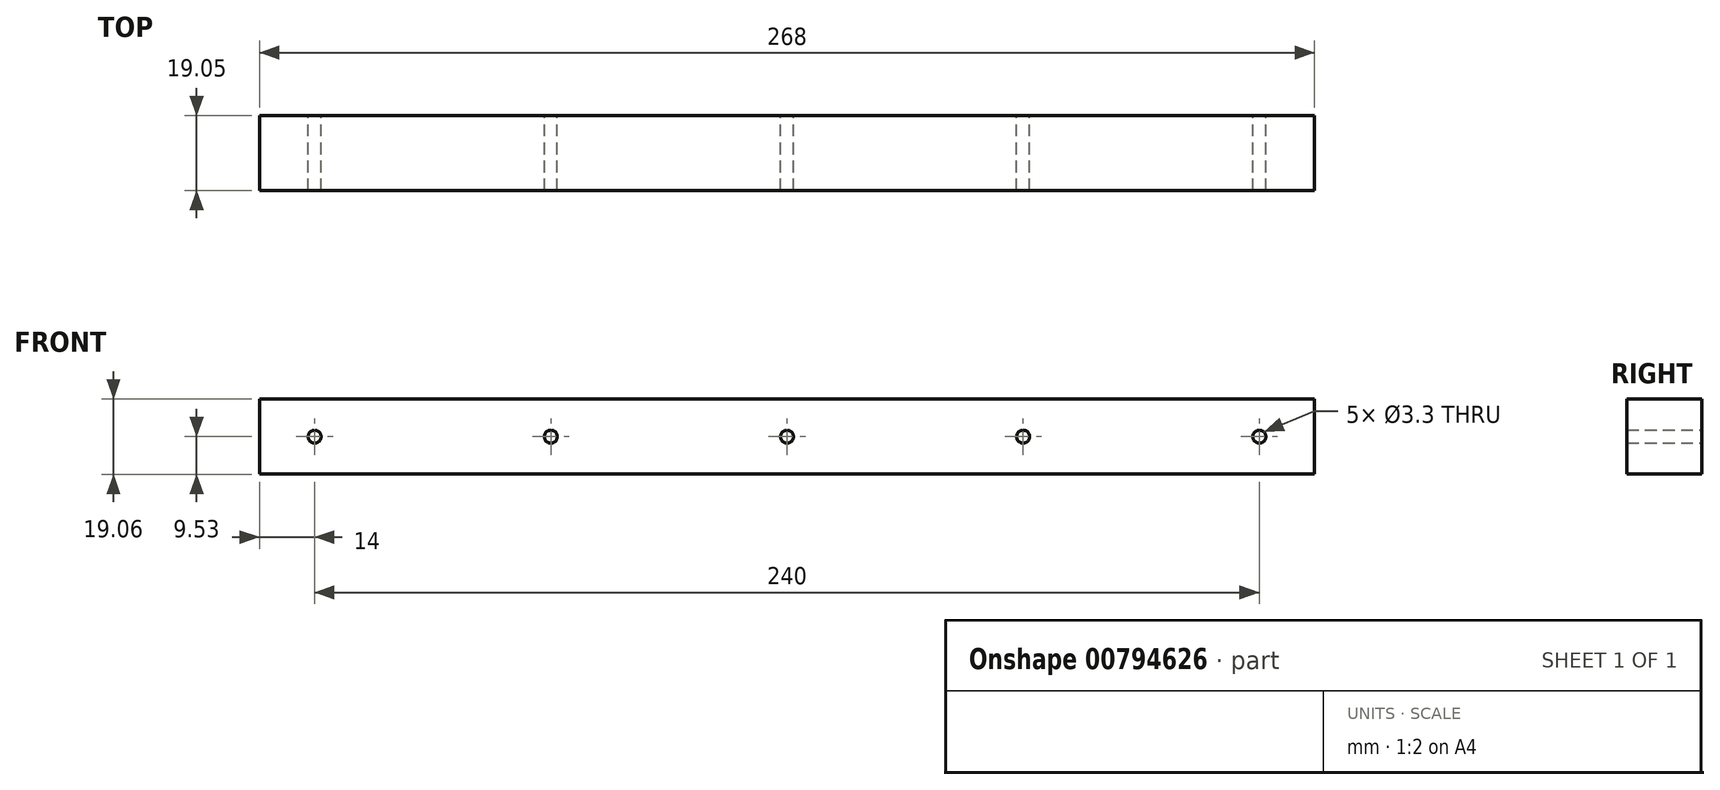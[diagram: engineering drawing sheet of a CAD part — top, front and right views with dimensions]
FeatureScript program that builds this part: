
annotation { "Feature Type Name" : "Feature", "Feature Type Description" : "" }
export const myFeature = defineFeature(function(context is Context, id is Id, definition is map)
    precondition{}
    {
        {
            var Q0;
            Q0=qCreatedBy(makeId("Front.planeOp"),FACE);
            var sketch = newSketch(context, id + "F0", { "sketchPlane" : qUnion([Q0])});
            skLineSegment(sketch, "E0.bottom", {"start": v(134, -9.52) * mm, "end": v(-134, -9.53) * mm});
            skLineSegment(sketch, "E0.top", {"start": v(134, 9.53) * mm, "end": v(-134, 9.52) * mm});
            skLineSegment(sketch, "E0.left", {"start": v(134, -9.52) * mm, "end": v(134, 9.53) * mm});
            skLineSegment(sketch, "E0.right", {"start": v(-134, -9.53) * mm, "end": v(-134, 9.52) * mm});
            skPoint(sketch, "E0.middle", {"position": v(0, 0) * mm});
            skSolve(sketch);
        }
        {
            var Q0;
            Q0 = qSketchRegion(id + "F0", true);
            extrude(context, id + "F1", {"entities" : qUnion([Q0]), "depth" : 19.05 * mm, "offsetDistance" : 25 * mm});
        }
        {
            var Q0;
            Q0=makeQuery(id+"F1.opExtrude","CAP_FACE",FACE,{"disambiguationData":[OSD([sQuery(id+"F0.wireOp",EDGE,"E0.bottom"),sQuery(id+"F0.wireOp",EDGE,"E0.top"),sQuery(id+"F0.wireOp",EDGE,"E0.left"),sQuery(id+"F0.wireOp",EDGE,"E0.right")])],"isStart":false});
            var sketch = newSketch(context, id + "F2", { "sketchPlane" : qUnion([Q0])});
            skLineSegment(sketch, "E1", {"start": v(-134, 0) * mm, "end": v(134, 0) * mm, "construction": true});
            skPoint(sketch, "E2", {"position": v(0, 0) * mm});
            skPoint(sketch, "E3", {"position": v(-60, 0) * mm});
            skPoint(sketch, "E4", {"position": v(-120, 0) * mm});
            skPoint(sketch, "E5", {"position": v(60, 0) * mm});
            skPoint(sketch, "E6", {"position": v(120, 0) * mm});
            skSolve(sketch);
        }
        {
            var Q0;
            Q0=sQuery(id+"F2.wireOp",VERTEX,"E4");
            var Q1;
            Q1=sQuery(id+"F2.wireOp",VERTEX,"E3");
            var Q2;
            Q2=sQuery(id+"F2.wireOp",VERTEX,"E2");
            var Q3;
            Q3=sQuery(id+"F2.wireOp",VERTEX,"E5");
            var Q4;
            Q4=sQuery(id+"F2.wireOp",VERTEX,"E6");
            var Q5;
            Q5=makeQuery(id+"F1.opExtrude","SWEPT_BODY",BODY,{"disambiguationData":[OSD([sQuery(id+"F0.wireOp",EDGE,"E0.bottom"),sQuery(id+"F0.wireOp",EDGE,"E0.top"),sQuery(id+"F0.wireOp",EDGE,"E0.left"),sQuery(id+"F0.wireOp",EDGE,"E0.right")])]});
            hole(context, id + "F3", {"style" : HoleStyle.SIMPLE, "endStyle" : HoleEndStyle.THROUGH, "standardTappedOrClearance" : lookupTablePath({ "standard" : "ISO", "engagement" : "75%", "pitch" : "0.7 mm", "size" : "M4", "type" : "Tapped" }), "standardBlindInLast" : lookupTablePath({ "standard" : "ISO", "engagement" : "75%", "pitch" : "0.7 mm", "size" : "M4", "type" : "Tapped" }), "holeDiameter" : 3.3 * mm, "majorDiameter" : 4 * mm, "showTappedDepth" : true, "isTappedThrough" : true, "tappedDepth" : 10.5 * mm, "tapClearance" : 3, "locations" : qUnion([Q0, Q1, Q2, Q3, Q4]), "scope" : qUnion([Q5]), "startStyle" : HoleStartStyle.SKETCH});
        }
    });
